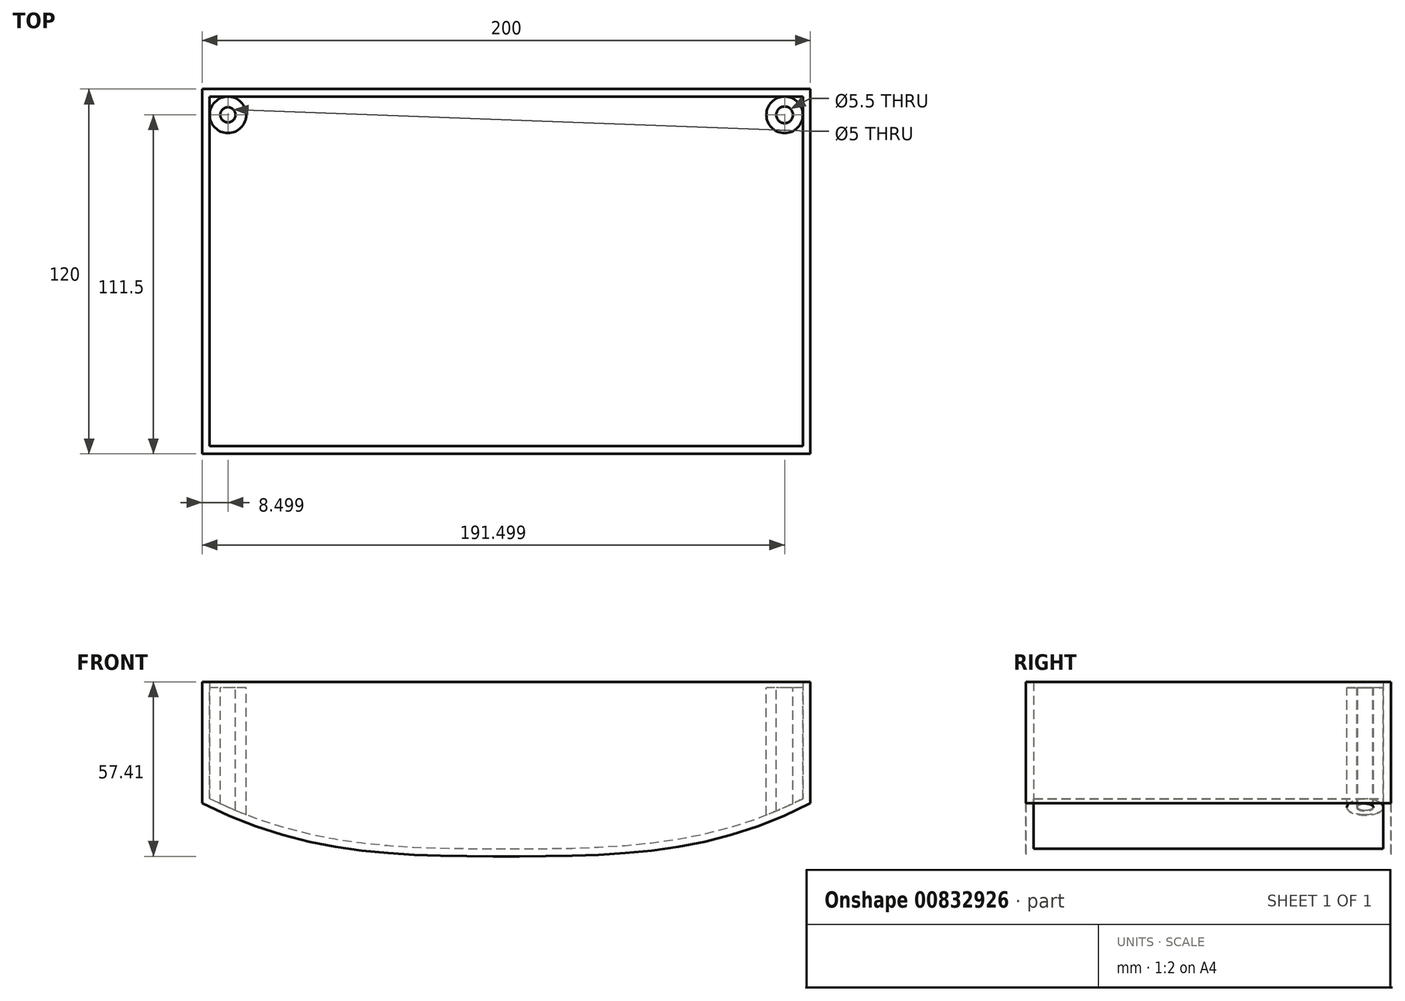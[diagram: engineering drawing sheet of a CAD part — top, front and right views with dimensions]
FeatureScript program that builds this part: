
annotation { "Feature Type Name" : "Feature", "Feature Type Description" : "" }
export const myFeature = defineFeature(function(context is Context, id is Id, definition is map)
    precondition{}
    {
        {
            var Q0;
            Q0=qCreatedBy(makeId("Front.planeOp"),FACE);
            var sketch = newSketch(context, id + "F0", { "sketchPlane" : qUnion([Q0])});
            skLineSegment(sketch, "E0.bottom", {"start": v(-132.4, 1.9) * mm, "end": v(67.6, 1.9) * mm});
            skLineSegment(sketch, "E0.left", {"start": v(-132.4, 1.9) * mm, "end": v(-132.4, -38.1) * mm});
            skLineSegment(sketch, "E0.right", {"start": v(67.6, 1.9) * mm, "end": v(67.6, -38.1) * mm});
            skFitSpline(sketch, "E1", {"points": [v(-132.4, -38.1) * mm, v(-32.4, -55.51) * mm, v(67.6, -38.1) * mm], "startDerivative": vector(204.98, -104.5) * mm, "endDerivative": vector(198.99, 104.5) * mm});
            skPoint(sketch, "E2.orphan", {"position": v(-132.4, -55.51) * mm});
            skPoint(sketch, "E3.orphan", {"position": v(67.6, -55.51) * mm});
            skSolve(sketch);
        }
        {
            var Q0;
            Q0=makeQuery(id+"F0.imprint","IMPRINT",FACE,{"disambiguationData":[TD([[makeQuery(id+"F0.imprint","IMPRINT",EDGE,{"derivedFrom":sQuery(id+"F0.wireOp",EDGE,"E0.bottom")}),-1.0]])]});
            extrude(context, id + "F1", {"entities" : qUnion([Q0]), "endBound" : BoundingType.SYMMETRIC, "depth" : 120 * mm, "offsetDistance" : 25 * mm});
        }
        {
            var Q0;
            Q0=makeQuery(id+"F1.opExtrude","SWEPT_FACE",FACE,{"disambiguationData":[OSD([sQuery(id+"F0.wireOp",EDGE,"E0.bottom")])]});
            shell(context, id + "F2", {"entities" : qUnion([Q0]), "thickness" : 2.5 * mm});
        }
        {
            var Q0;
            Q0=qCreatedBy(makeId("Top.planeOp"),FACE);
            var sketch = newSketch(context, id + "F3", { "sketchPlane" : qUnion([Q0])});
            skCircle(sketch, "E4", {"center": v(59.1, 51.5) * mm, "radius": 6 * mm});
            skCircle(sketch, "E5", {"center": v(59.1, 51.5) * mm, "radius": 2.75 * mm});
            skCircle(sketch, "E6.MirrorC", {"center": v(59.1, -51.5) * mm, "radius": 6 * mm});
            skCircle(sketch, "E7.MirrorC", {"center": v(59.1, -51.5) * mm, "radius": 2.75 * mm});
            skCircle(sketch, "E8", {"center": v(-123.9, 51.5) * mm, "radius": 2.5 * mm});
            skCircle(sketch, "E9", {"center": v(-123.9, 51.5) * mm, "radius": 6 * mm});
            skCircle(sketch, "E10.MirrorC", {"center": v(-123.9, -51.5) * mm, "radius": 6 * mm});
            skCircle(sketch, "E11.MirrorC", {"center": v(-123.9, -51.5) * mm, "radius": 2.5 * mm});
            skSolve(sketch);
        }
        {
            var Q0;
            Q0=makeQuery(id+"F3.imprint","IMPRINT",FACE,{"disambiguationData":[TD([[makeQuery(id+"F3.imprint","IMPRINT",EDGE,{"derivedFrom":sQuery(id+"F3.wireOp",EDGE,"E8")}),-1.0]])]});
            var Q1;
            Q1=makeQuery(id+"F3.imprint","IMPRINT",FACE,{"disambiguationData":[TD([[makeQuery(id+"F3.imprint","IMPRINT",EDGE,{"derivedFrom":sQuery(id+"F3.wireOp",EDGE,"E4")}),1.0]])]});
            var Q2;
            Q2=makeQuery(id+"F3.imprint","IMPRINT",FACE,{"disambiguationData":[TD([[makeQuery(id+"F3.imprint","IMPRINT",EDGE,{"derivedFrom":sQuery(id+"F3.wireOp",EDGE,"E6.MirrorC")}),-1.0]])]});
            var Q3;
            Q3=makeQuery(id+"F3.imprint","IMPRINT",FACE,{"disambiguationData":[TD([[makeQuery(id+"F3.imprint","IMPRINT",EDGE,{"derivedFrom":sQuery(id+"F3.wireOp",EDGE,"E10.MirrorC")}),-1.0]])]});
            extrude(context, id + "F4", {"entities" : qUnion([Q0, Q1, Q2, Q3]), "endBound" : BoundingType.UP_TO_NEXT, "oppositeDirection" : true, "depth" : 25 * mm, "offsetDistance" : 25 * mm});
        }
    });
